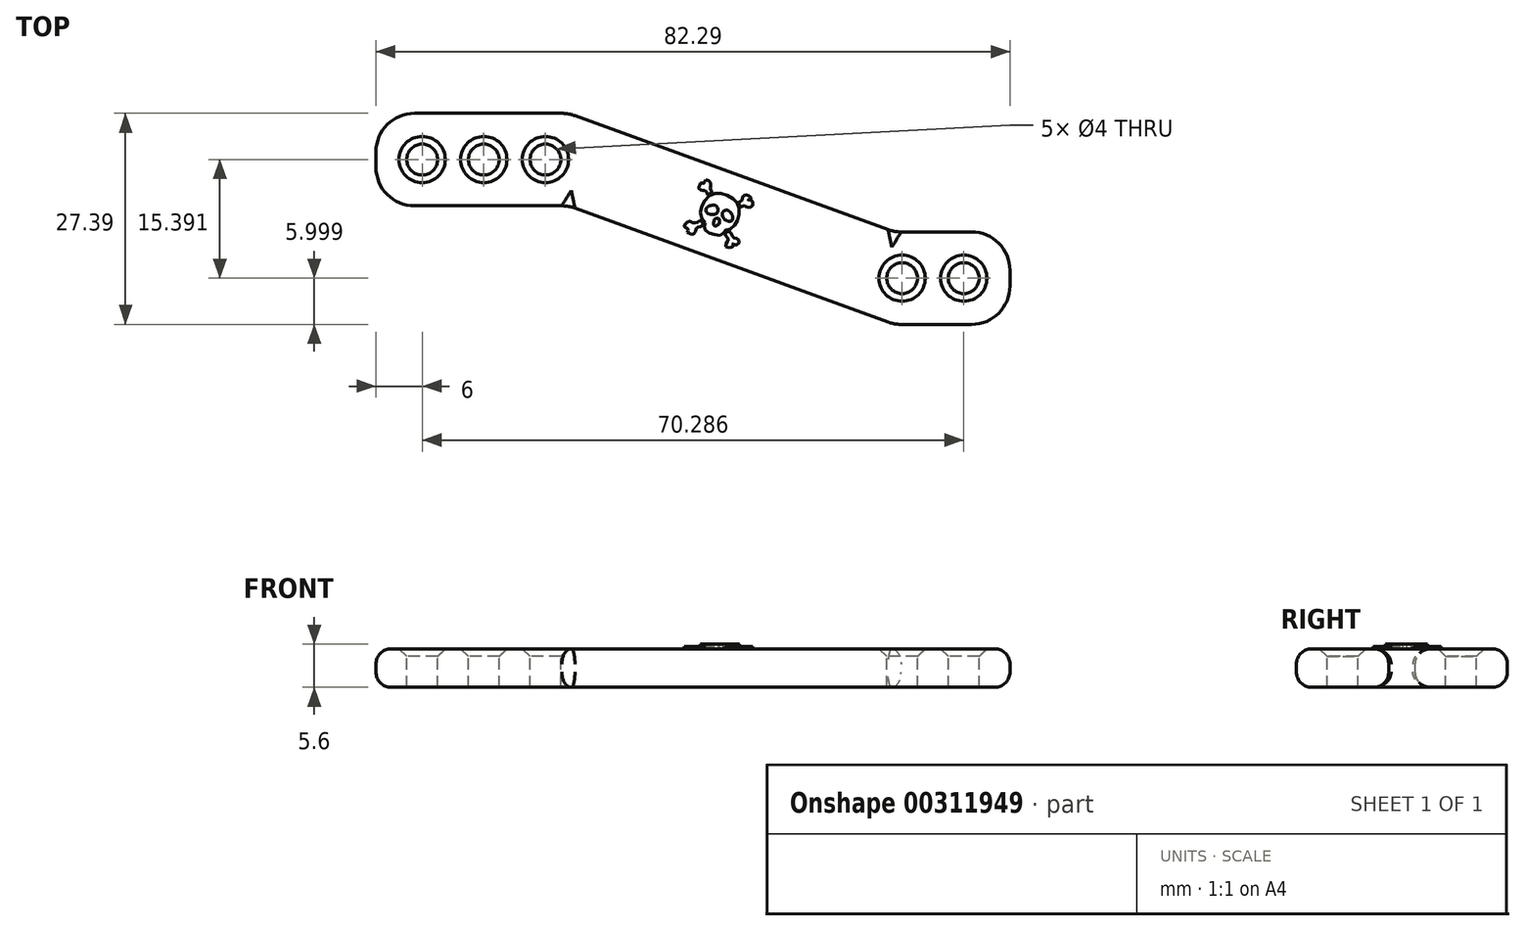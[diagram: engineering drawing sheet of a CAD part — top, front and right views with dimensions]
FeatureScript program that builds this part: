
annotation { "Feature Type Name" : "Feature", "Feature Type Description" : "" }
export const myFeature = defineFeature(function(context is Context, id is Id, definition is map)
    precondition{}
    {
        {
            var Q0;
            Q0=qCreatedBy(makeId("Top.planeOp"),FACE);
            var sketch = newSketch(context, id + "F0", { "sketchPlane" : qUnion([Q0])});
            skLineSegment(sketch, "E0.bottom", {"start": v(0, 12) * mm, "end": v(25, 12) * mm});
            skLineSegment(sketch, "E0.top", {"start": v(0, 0) * mm, "end": v(25, 0) * mm});
            skLineSegment(sketch, "E0.left", {"start": v(0, 12) * mm, "end": v(0, 0) * mm});
            skLineSegment(sketch, "E0.right", {"start": v(25, 12) * mm, "end": v(25, 0) * mm});
            skLineSegment(sketch, "E1.bottom", {"start": v(67.29, -3.4) * mm, "end": v(82.29, -3.4) * mm});
            skLineSegment(sketch, "E1.top", {"start": v(67.29, -15.4) * mm, "end": v(82.29, -15.4) * mm});
            skLineSegment(sketch, "E1.left", {"start": v(67.29, -3.4) * mm, "end": v(67.29, -15.4) * mm});
            skLineSegment(sketch, "E1.right", {"start": v(82.29, -3.4) * mm, "end": v(82.29, -15.4) * mm});
            skLineSegment(sketch, "E2", {"start": v(25, 12) * mm, "end": v(67.29, -3.4) * mm});
            skLineSegment(sketch, "E3", {"start": v(25, 0) * mm, "end": v(67.29, -15.4) * mm});
            skSolve(sketch);
        }
        {
            var Q0;
            Q0=makeQuery(id+"F0.imprint","IMPRINT",FACE,{"disambiguationData":[TD([[makeQuery(id+"F0.imprint","IMPRINT",EDGE,{"derivedFrom":sQuery(id+"F0.wireOp",EDGE,"E0.bottom")}),-1.0]])]});
            var Q1;
            Q1=makeQuery(id+"F0.imprint","IMPRINT",FACE,{"disambiguationData":[TD([[makeQuery(id+"F0.imprint","IMPRINT",EDGE,{"derivedFrom":sQuery(id+"F0.wireOp",EDGE,"E1.bottom")}),-1.0]])]});
            var Q2;
            Q2=makeQuery(id+"F0.imprint","IMPRINT",FACE,{"disambiguationData":[TD([[makeQuery(id+"F0.imprint","IMPRINT",EDGE,{"derivedFrom":sQuery(id+"F0.wireOp",EDGE,"E0.right")}),1.0]])]});
            extrude(context, id + "F1", {"entities" : qUnion([Q0, Q1, Q2]), "depth" : 5 * mm});
        }
        {
            var Q0;
            Q0=makeQuery(id+"F1.opExtrude","CAP_FACE",FACE,{"disambiguationData":[OSD([sQuery(id+"F0.wireOp",EDGE,"E0.bottom"),sQuery(id+"F0.wireOp",EDGE,"E0.top"),sQuery(id+"F0.wireOp",EDGE,"E0.left"),sQuery(id+"F0.wireOp",EDGE,"E1.bottom"),sQuery(id+"F0.wireOp",EDGE,"E1.top"),sQuery(id+"F0.wireOp",EDGE,"E1.right"),sQuery(id+"F0.wireOp",EDGE,"E2"),sQuery(id+"F0.wireOp",EDGE,"E3")])],"isStart":false});
            var sketch = newSketch(context, id + "F2", { "sketchPlane" : qUnion([Q0])});
            skCircle(sketch, "E4", {"center": v(6, 6) * mm, "radius": 2 * mm});
            skCircle(sketch, "E5", {"center": v(76.29, -9.4) * mm, "radius": 2 * mm});
            skCircle(sketch, "E6.1.0.0", {"center": v(14, 6) * mm, "radius": 2 * mm});
            skCircle(sketch, "E6.2.0.0", {"center": v(22, 6) * mm, "radius": 2 * mm});
            skLineSegment(sketch, "E6.direction1", {"start": v(6, 6) * mm, "end": v(14, 6) * mm, "construction": true});
            skCircle(sketch, "E7.1.0.0", {"center": v(68.29, -9.4) * mm, "radius": 2 * mm});
            skLineSegment(sketch, "E7.direction1", {"start": v(76.29, -9.4) * mm, "end": v(68.29, -9.4) * mm, "construction": true});
            skSolve(sketch);
        }
        {
            var Q0;
            Q0 = qSketchRegion(id + "F2", true);
            extrude(context, id + "F3", {"entities" : qUnion([Q0]), "operationType" : NewBodyOperationType.REMOVE, "oppositeDirection" : true, "depth" : 5 * mm});
        }
        {
            var Q0;
            Q0=makeQuery(id+"F1.opExtrude","CAP_EDGE",EDGE,{"disambiguationData":[OSD([sQuery(id+"F0.wireOp",EDGE,"E3")])],"isStart":false});
            var Q1;
            Q1=makeQuery(id+"F1.opExtrude","CAP_EDGE",EDGE,{"disambiguationData":[OSD([sQuery(id+"F0.wireOp",EDGE,"E1.top")])],"isStart":false});
            var Q2;
            Q2=makeQuery(id+"F1.opExtrude","CAP_EDGE",EDGE,{"disambiguationData":[OSD([sQuery(id+"F0.wireOp",EDGE,"E1.right")])],"isStart":false});
            var Q3;
            Q3=makeQuery(id+"F1.opExtrude","CAP_EDGE",EDGE,{"disambiguationData":[OSD([sQuery(id+"F0.wireOp",EDGE,"E1.bottom")])],"isStart":false});
            var Q4;
            Q4=makeQuery(id+"F1.opExtrude","CAP_EDGE",EDGE,{"disambiguationData":[OSD([sQuery(id+"F0.wireOp",EDGE,"E2")])],"isStart":false});
            var Q5;
            Q5=makeQuery(id+"F1.opExtrude","CAP_EDGE",EDGE,{"disambiguationData":[OSD([sQuery(id+"F0.wireOp",EDGE,"E0.bottom")])],"isStart":false});
            var Q6;
            Q6=makeQuery(id+"F1.opExtrude","CAP_EDGE",EDGE,{"disambiguationData":[OSD([sQuery(id+"F0.wireOp",EDGE,"E0.left")])],"isStart":false});
            var Q7;
            Q7=makeQuery(id+"F1.opExtrude","CAP_EDGE",EDGE,{"disambiguationData":[OSD([sQuery(id+"F0.wireOp",EDGE,"E0.top")])],"isStart":false});
            var Q8;
            Q8=makeQuery(id+"F1.opExtrude","CAP_EDGE",EDGE,{"disambiguationData":[OSD([sQuery(id+"F0.wireOp",EDGE,"E0.left")])],"isStart":true});
            var Q9;
            Q9=makeQuery(id+"F1.opExtrude","CAP_EDGE",EDGE,{"disambiguationData":[OSD([sQuery(id+"F0.wireOp",EDGE,"E0.top")])],"isStart":true});
            var Q10;
            Q10=makeQuery(id+"F1.opExtrude","CAP_EDGE",EDGE,{"disambiguationData":[OSD([sQuery(id+"F0.wireOp",EDGE,"E1.right")])],"isStart":true});
            var Q11;
            Q11=makeQuery(id+"F1.opExtrude","CAP_EDGE",EDGE,{"disambiguationData":[OSD([sQuery(id+"F0.wireOp",EDGE,"E1.bottom")])],"isStart":true});
            var Q12;
            Q12=makeQuery(id+"F1.opExtrude","CAP_EDGE",EDGE,{"disambiguationData":[OSD([sQuery(id+"F0.wireOp",EDGE,"E0.bottom")])],"isStart":true});
            var Q13;
            Q13=makeQuery(id+"F1.opExtrude","CAP_EDGE",EDGE,{"disambiguationData":[OSD([sQuery(id+"F0.wireOp",EDGE,"E2")])],"isStart":true});
            var Q14;
            Q14=makeQuery(id+"F1.opExtrude","CAP_EDGE",EDGE,{"disambiguationData":[OSD([sQuery(id+"F0.wireOp",EDGE,"E3")])],"isStart":true});
            var Q15;
            Q15=makeQuery(id+"F1.opExtrude","CAP_EDGE",EDGE,{"disambiguationData":[OSD([sQuery(id+"F0.wireOp",EDGE,"E1.top")])],"isStart":true});
            fillet(context, id + "F4", {"entities" : qUnion([Q0, Q1, Q2, Q3, Q4, Q5, Q6, Q7, Q8, Q9, Q10, Q11, Q12, Q13, Q14, Q15]), "radius" : 2 * mm, "tangentPropagation" : true, "allowEdgeOverflow" : false});
        }
        {
            var Q0;
            Q0=makeQuery(id+"F1.opExtrude","SWEPT_EDGE",EDGE,{"disambiguationData":[OSD([sQuery(id+"F0.wireOp",EDGE,"E0.top"),sQuery(id+"F0.wireOp",EDGE,"E0.left")])]});
            var Q1;
            Q1=makeQuery(id+"F1.opExtrude","SWEPT_EDGE",EDGE,{"disambiguationData":[OSD([sQuery(id+"F0.wireOp",EDGE,"E0.bottom"),sQuery(id+"F0.wireOp",EDGE,"E0.left")])]});
            var Q2;
            Q2=makeQuery(id+"F1.opExtrude","SWEPT_EDGE",EDGE,{"disambiguationData":[OSD([sQuery(id+"F0.wireOp",EDGE,"E1.top"),sQuery(id+"F0.wireOp",EDGE,"E1.left"),sQuery(id+"F0.wireOp",EDGE,"E3")])]});
            var Q3;
            Q3=makeQuery(id+"F1.opExtrude","SWEPT_EDGE",EDGE,{"disambiguationData":[OSD([sQuery(id+"F0.wireOp",EDGE,"E1.bottom"),sQuery(id+"F0.wireOp",EDGE,"E1.right")])]});
            var Q4;
            Q4=makeQuery(id+"F1.opExtrude","SWEPT_EDGE",EDGE,{"disambiguationData":[OSD([sQuery(id+"F0.wireOp",EDGE,"E1.bottom"),sQuery(id+"F0.wireOp",EDGE,"E1.left"),sQuery(id+"F0.wireOp",EDGE,"E2")])]});
            var Q5;
            Q5=makeQuery(id+"F1.opExtrude","SWEPT_EDGE",EDGE,{"disambiguationData":[OSD([sQuery(id+"F0.wireOp",EDGE,"E0.bottom"),sQuery(id+"F0.wireOp",EDGE,"E0.right"),sQuery(id+"F0.wireOp",EDGE,"E2")])]});
            var Q6;
            Q6=makeQuery(id+"F1.opExtrude","SWEPT_EDGE",EDGE,{"disambiguationData":[OSD([sQuery(id+"F0.wireOp",EDGE,"E0.top"),sQuery(id+"F0.wireOp",EDGE,"E0.right"),sQuery(id+"F0.wireOp",EDGE,"E3")])]});
            var Q7;
            Q7=makeQuery(id+"F1.opExtrude","SWEPT_EDGE",EDGE,{"disambiguationData":[OSD([sQuery(id+"F0.wireOp",EDGE,"E1.top"),sQuery(id+"F0.wireOp",EDGE,"E1.right")])]});
            fillet(context, id + "F5", {"entities" : qUnion([Q0, Q1, Q2, Q3, Q4, Q5, Q6, Q7]), "radius" : 5 * mm, "tangentPropagation" : true, "allowEdgeOverflow" : false});
        }
        {
            var Q0;
            Q0=makeQuery(id+"F1.opExtrude","CAP_FACE",FACE,{"disambiguationData":[OSD([sQuery(id+"F0.wireOp",EDGE,"E0.bottom"),sQuery(id+"F0.wireOp",EDGE,"E0.top"),sQuery(id+"F0.wireOp",EDGE,"E0.left"),sQuery(id+"F0.wireOp",EDGE,"E1.bottom"),sQuery(id+"F0.wireOp",EDGE,"E1.top"),sQuery(id+"F0.wireOp",EDGE,"E1.right"),sQuery(id+"F0.wireOp",EDGE,"E2"),sQuery(id+"F0.wireOp",EDGE,"E3")])],"isStart":false});
            chamfer(context, id + "F6", {"entities" : qUnion([Q0]), "width" : 1 * mm, "tangentPropagation" : true});
        }
        {
            var Q0;
            Q0=makeQuery(id+"F1.opExtrude","CAP_FACE",FACE,{"disambiguationData":[OSD([sQuery(id+"F0.wireOp",EDGE,"E0.bottom"),sQuery(id+"F0.wireOp",EDGE,"E0.top"),sQuery(id+"F0.wireOp",EDGE,"E0.left"),sQuery(id+"F0.wireOp",EDGE,"E1.bottom"),sQuery(id+"F0.wireOp",EDGE,"E1.top"),sQuery(id+"F0.wireOp",EDGE,"E1.right"),sQuery(id+"F0.wireOp",EDGE,"E2"),sQuery(id+"F0.wireOp",EDGE,"E3")])],"isStart":false});
            var sketch = newSketch(context, id + "F7", { "sketchPlane" : qUnion([Q0])});
            skPoint(sketch, "E8.8.internal.snap0", {"position": v(41.12, 0.13) * mm});
            skFitSpline(sketch, "E8", {"points": [v(42.7, -2.2) * mm, v(42.25, -1.55) * mm, v(42.17, -0.46) * mm, v(42.59, 0.58) * mm, v(43.4, 1.38) * mm, v(44.4, 1.62) * mm, v(45.56, 1.36) * mm, v(46.55, 0.75) * mm, v(47.01, 0.13) * mm, v(47.16, -0.92) * mm, v(46.9, -1.91) * mm, v(46.39, -2.68) * mm, v(45.66, -3.14) * mm, v(45.27, -3.2) * mm, v(44.98, -3.68) * mm, v(44.47, -3.82) * mm, v(43.65, -3.65) * mm, v(42.97, -3.34) * mm, v(42.61, -2.9) * mm, v(42.63, -2.47) * mm, v(42.7, -2.2) * mm]});
            skFitSpline(sketch, "E9", {"points": [v(40.5, -3.03) * mm, v(40.06, -2.79) * mm, v(40.25, -2.26) * mm, v(40.8, -2.01) * mm, v(41.11, -2.23) * mm, v(41.76, -2.08) * mm, v(42.2, -1.91) * mm, v(42.4, -2.18) * mm, v(42.3, -2.64) * mm, v(41.76, -2.78) * mm, v(41.55, -2.98) * mm, v(41.42, -3.36) * mm, v(41.02, -3.7) * mm, v(40.63, -3.56) * mm, v(40.42, -3.48) * mm, v(40.5, -3.03) * mm]});
            skFitSpline(sketch, "E10", {"points": [v(42.59, 2.95) * mm, v(42.15, 2.97) * mm, v(42.04, 2.65) * mm, v(41.91, 2.3) * mm, v(42.32, 2) * mm, v(42.7, 2) * mm, v(43, 1.62) * mm, v(43.1, 1.38) * mm, v(43.4, 1.64) * mm, v(43.63, 1.72) * mm, v(43.4, 2.2) * mm, v(43.4, 2.37) * mm, v(43.4, 2.85) * mm, v(43.18, 3.25) * mm, v(42.79, 3.4) * mm, v(42.59, 2.95) * mm]});
            skFitSpline(sketch, "E11", {"points": [v(47.01, 0.41) * mm, v(47.52, 0.8) * mm, v(47.72, 1.3) * mm, v(48.37, 1.3) * mm, v(48.66, 0.9) * mm, v(48.27, 0.78) * mm, v(48.76, 0.68) * mm, v(48.92, 0.29) * mm, v(48.8, -0.05) * mm, v(48.27, -0.22) * mm, v(47.86, 0) * mm, v(47.3, -0.17) * mm], "startDerivative": vector(5.39, 3.3) * mm, "endDerivative": vector(-9.27, -3.63) * mm});
            skFitSpline(sketch, "E12", {"points": [v(45.27, -3.68) * mm, v(45.54, -3.39) * mm, v(45.9, -3.39) * mm, v(46.17, -3.68) * mm, v(46.39, -4.11) * mm, v(46.85, -4.26) * mm, v(47.14, -4.62) * mm, v(47.03, -4.92) * mm, v(46.6, -5.1) * mm, v(46.34, -4.91) * mm, v(46.39, -5.18) * mm, v(46.17, -5.35) * mm, v(45.83, -5.45) * mm, v(45.38, -5.3) * mm, v(45.56, -4.77) * mm, v(45.68, -4.23) * mm, v(45.27, -3.68) * mm]});
            skFitSpline(sketch, "E13", {"points": [v(42.95, -0.22) * mm, v(43.43, 0.05) * mm, v(43.99, 0.07) * mm, v(44.35, -0.36) * mm, v(44.2, -1) * mm, v(43.72, -1.11) * mm, v(43.12, -1.02) * mm, v(42.83, -0.7) * mm, v(42.95, -0.22) * mm]});
            skFitSpline(sketch, "E14", {"points": [v(45.13, -0.68) * mm, v(45.61, -0.56) * mm, v(46.05, -0.92) * mm, v(46.29, -1.4) * mm, v(46.14, -1.96) * mm, v(45.54, -1.94) * mm, v(45.03, -1.48) * mm, v(44.98, -0.94) * mm, v(45.13, -0.68) * mm]});
            skFitSpline(sketch, "E15", {"points": [v(44.06, -1.65) * mm, v(44.45, -1.65) * mm, v(44.6, -2.1) * mm, v(44.35, -2.5) * mm, v(43.99, -2.61) * mm, v(43.8, -2.3) * mm, v(43.92, -1.84) * mm, v(44.06, -1.65) * mm]});
            skFitSpline(sketch, "E16", {"points": [v(47.01, 0.41) * mm, v(47.17, 0.13) * mm, v(47.3, -0.17) * mm], "startDerivative": vector(0.33, -0.55) * mm, "endDerivative": vector(0.25, -0.6) * mm});
            skSolve(sketch);
        }
        {
            var Q0;
            Q0=makeQuery(id+"F7.imprint","IMPRINT",FACE,{"disambiguationData":[TD([[makeQuery(id+"F7.imprint","IMPRINT",EDGE,{"derivedFrom":sQuery(id+"F7.wireOp",EDGE,"E8")}),-1.0]])]});
            extrude(context, id + "F8", {"entities" : qUnion([Q0]), "operationType" : NewBodyOperationType.ADD, "depth" : .6 * mm});
        }
        {
            var Q0;
            {var subQ0=sQuery(id+"F7.wireOp",EDGE,"E9");var subQ1=sQuery(id+"F0.wireOp",EDGE,"E3");var subQ2=makeQuery(id+"F4.opFillet","BLEND_EDGE",EDGE,{"blendedFrom":[makeQuery(id+"F1.opExtrude","CAP_EDGE",EDGE,{"disambiguationData":[OSD([subQ1])],"isStart":false}),makeQuery(id+"F1.opExtrude","CAP_FACE",FACE,{"disambiguationData":[OSD([sQuery(id+"F0.wireOp",EDGE,"E0.bottom"),sQuery(id+"F0.wireOp",EDGE,"E0.top"),sQuery(id+"F0.wireOp",EDGE,"E0.left"),sQuery(id+"F0.wireOp",EDGE,"E1.bottom"),sQuery(id+"F0.wireOp",EDGE,"E1.top"),sQuery(id+"F0.wireOp",EDGE,"E1.right"),sQuery(id+"F0.wireOp",EDGE,"E2"),subQ1])],"isStart":false})],"blendedInto":[makeQuery(id+"F1.opExtrude","CAP_FACE",FACE,{"disambiguationData":[OSD([sQuery(id+"F0.wireOp",EDGE,"E0.bottom"),sQuery(id+"F0.wireOp",EDGE,"E0.top"),sQuery(id+"F0.wireOp",EDGE,"E0.left"),sQuery(id+"F0.wireOp",EDGE,"E1.bottom"),sQuery(id+"F0.wireOp",EDGE,"E1.top"),sQuery(id+"F0.wireOp",EDGE,"E1.right"),sQuery(id+"F0.wireOp",EDGE,"E2"),subQ1])],"isStart":false})]});var subQ3=makeQuery(id+"F7.imprint","INTERSECT",VERTEX,{"disambiguationData":[OD(0.0)],"derivedFrom":[subQ2,subQ0]});Q0=makeQuery(id+"F7.imprint","IMPRINT",FACE,{"disambiguationData":[TD([[makeQuery(id+"F7.imprint","IMPRINT",EDGE,{"disambiguationData":[TD([[subQ3,-1.0]])],"derivedFrom":subQ0}),-1.0]])]});}
            var Q1;
            {var subQ0=sQuery(id+"F7.wireOp",EDGE,"E10");var subQ1=sQuery(id+"F0.wireOp",EDGE,"E2");var subQ2=makeQuery(id+"F4.opFillet","BLEND_EDGE",EDGE,{"blendedFrom":[makeQuery(id+"F1.opExtrude","CAP_EDGE",EDGE,{"disambiguationData":[OSD([subQ1])],"isStart":false}),makeQuery(id+"F1.opExtrude","CAP_FACE",FACE,{"disambiguationData":[OSD([sQuery(id+"F0.wireOp",EDGE,"E0.bottom"),sQuery(id+"F0.wireOp",EDGE,"E0.top"),sQuery(id+"F0.wireOp",EDGE,"E0.left"),sQuery(id+"F0.wireOp",EDGE,"E1.bottom"),sQuery(id+"F0.wireOp",EDGE,"E1.top"),sQuery(id+"F0.wireOp",EDGE,"E1.right"),subQ1,sQuery(id+"F0.wireOp",EDGE,"E3")])],"isStart":false})],"blendedInto":[makeQuery(id+"F1.opExtrude","CAP_FACE",FACE,{"disambiguationData":[OSD([sQuery(id+"F0.wireOp",EDGE,"E0.bottom"),sQuery(id+"F0.wireOp",EDGE,"E0.top"),sQuery(id+"F0.wireOp",EDGE,"E0.left"),sQuery(id+"F0.wireOp",EDGE,"E1.bottom"),sQuery(id+"F0.wireOp",EDGE,"E1.top"),sQuery(id+"F0.wireOp",EDGE,"E1.right"),subQ1,sQuery(id+"F0.wireOp",EDGE,"E3")])],"isStart":false})]});var subQ3=makeQuery(id+"F7.imprint","INTERSECT",VERTEX,{"disambiguationData":[OD(0.0)],"derivedFrom":[subQ2,subQ0]});Q1=makeQuery(id+"F7.imprint","IMPRINT",FACE,{"disambiguationData":[TD([[makeQuery(id+"F7.imprint","IMPRINT",EDGE,{"disambiguationData":[TD([[subQ3,-1.0]])],"derivedFrom":subQ0}),1.0]])]});}
            var Q2;
            Q2=makeQuery(id+"F7.imprint","IMPRINT",FACE,{"disambiguationData":[TD([[makeQuery(id+"F7.imprint","IMPRINT",EDGE,{"derivedFrom":sQuery(id+"F7.wireOp",EDGE,"E11")}),-1.0]])]});
            var Q3;
            {var subQ0=sQuery(id+"F7.wireOp",EDGE,"E12");var subQ1=sQuery(id+"F0.wireOp",EDGE,"E3");var subQ2=makeQuery(id+"F4.opFillet","BLEND_EDGE",EDGE,{"blendedFrom":[makeQuery(id+"F1.opExtrude","CAP_EDGE",EDGE,{"disambiguationData":[OSD([subQ1])],"isStart":false}),makeQuery(id+"F1.opExtrude","CAP_FACE",FACE,{"disambiguationData":[OSD([sQuery(id+"F0.wireOp",EDGE,"E0.bottom"),sQuery(id+"F0.wireOp",EDGE,"E0.top"),sQuery(id+"F0.wireOp",EDGE,"E0.left"),sQuery(id+"F0.wireOp",EDGE,"E1.bottom"),sQuery(id+"F0.wireOp",EDGE,"E1.top"),sQuery(id+"F0.wireOp",EDGE,"E1.right"),sQuery(id+"F0.wireOp",EDGE,"E2"),subQ1])],"isStart":false})],"blendedInto":[makeQuery(id+"F1.opExtrude","CAP_FACE",FACE,{"disambiguationData":[OSD([sQuery(id+"F0.wireOp",EDGE,"E0.bottom"),sQuery(id+"F0.wireOp",EDGE,"E0.top"),sQuery(id+"F0.wireOp",EDGE,"E0.left"),sQuery(id+"F0.wireOp",EDGE,"E1.bottom"),sQuery(id+"F0.wireOp",EDGE,"E1.top"),sQuery(id+"F0.wireOp",EDGE,"E1.right"),sQuery(id+"F0.wireOp",EDGE,"E2"),subQ1])],"isStart":false})]});var subQ3=makeQuery(id+"F7.imprint","INTERSECT",VERTEX,{"disambiguationData":[OD(0.0)],"derivedFrom":[subQ2,subQ0]});Q3=makeQuery(id+"F7.imprint","IMPRINT",FACE,{"disambiguationData":[TD([[makeQuery(id+"F7.imprint","IMPRINT",EDGE,{"disambiguationData":[TD([[subQ3,1.0]])],"derivedFrom":subQ0}),-1.0]])]});}
            extrude(context, id + "F9", {"entities" : qUnion([Q0, Q1, Q2, Q3]), "operationType" : NewBodyOperationType.ADD, "depth" : .3 * mm});
        }
    });
